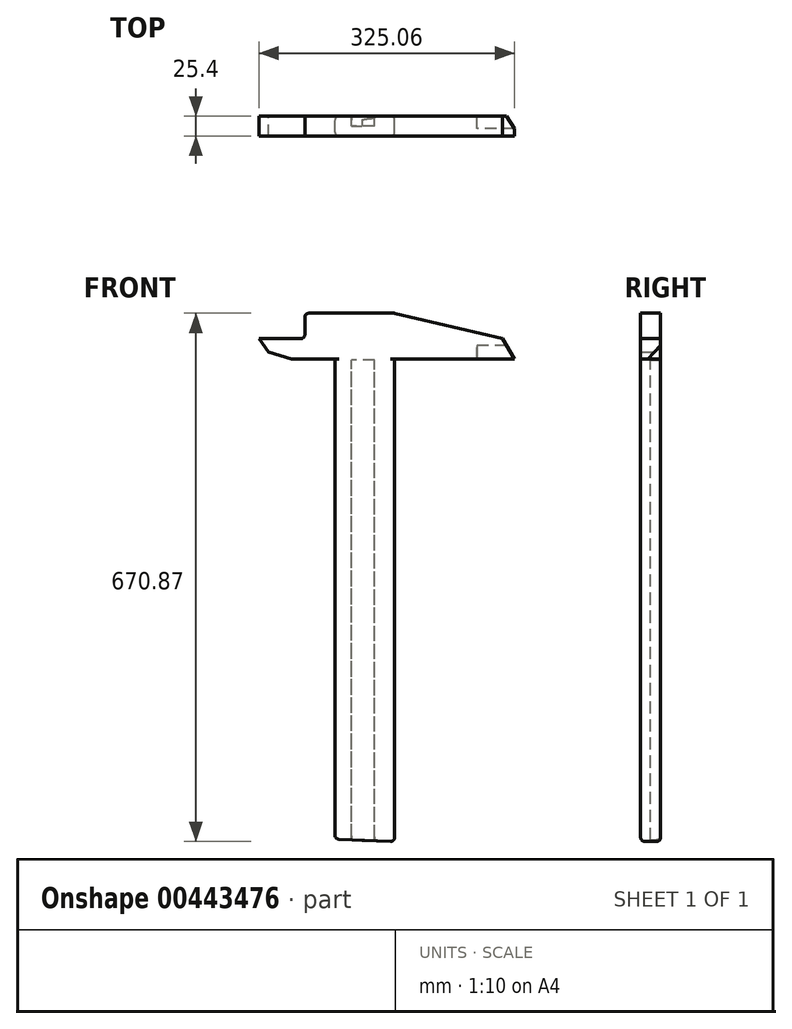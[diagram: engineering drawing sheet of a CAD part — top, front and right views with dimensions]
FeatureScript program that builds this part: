
annotation { "Feature Type Name" : "Feature", "Feature Type Description" : "" }
export const myFeature = defineFeature(function(context is Context, id is Id, definition is map)
    precondition{}
    {
        {
            var Q0;
            Q0=qCreatedBy(makeId("Front.planeOp"),FACE);
            var sketch = newSketch(context, id + "F0", { "sketchPlane" : qUnion([Q0])});
            skLineSegment(sketch, "E0", {"start": v(0, 0) * mm, "end": v(0, 114.3) * mm, "construction": true});
            skLineSegment(sketch, "E1", {"start": v(0, 114.3) * mm, "end": v(-53.98, 114.3) * mm, "construction": true});
            skLineSegment(sketch, "E2", {"start": v(-53.98, 114.3) * mm, "end": v(47.63, 114.3) * mm});
            skLineSegment(sketch, "E3", {"start": v(-53.98, 114.3) * mm, "end": v(-104.78, 114.3) * mm});
            skLineSegment(sketch, "E4", {"start": v(47.63, 114.3) * mm, "end": v(31.96, 140.42) * mm});
            skLineSegment(sketch, "E5", {"start": v(31.96, 140.42) * mm, "end": v(-105.1, 172.67) * mm});
            skLineSegment(sketch, "E6", {"start": v(-105.1, 172.67) * mm, "end": v(-218.99, 172.67) * mm});
            skLineSegment(sketch, "E7", {"start": v(-218.99, 172.67) * mm, "end": v(-218.99, 140.42) * mm});
            skLineSegment(sketch, "E8", {"start": v(-218.99, 140.42) * mm, "end": v(-277.44, 140.42) * mm});
            skLineSegment(sketch, "E9", {"start": v(-277.44, 140.42) * mm, "end": v(-265.35, 123.28) * mm});
            skLineSegment(sketch, "E10", {"start": v(-265.35, 123.28) * mm, "end": v(-235.11, 114.3) * mm});
            skLineSegment(sketch, "E11", {"start": v(-235.11, 114.3) * mm, "end": v(-180.7, 114.3) * mm});
            skLineSegment(sketch, "E12", {"start": v(-180.7, 114.3) * mm, "end": v(-180.7, -292.1) * mm});
            skLineSegment(sketch, "E13", {"start": v(-104.78, -292.1) * mm, "end": v(-104.78, 114.3) * mm});
            skLineSegment(sketch, "E14", {"start": v(-180.7, -292.1) * mm, "end": v(-180.7, -495.3) * mm});
            skLineSegment(sketch, "E15", {"start": v(-104.78, -292.1) * mm, "end": v(-104.77, -498.4) * mm});
            skLineSegment(sketch, "E16", {"start": v(-104.77, -498.4) * mm, "end": v(-180.7, -495.3) * mm});
            skSolve(sketch);
        }
        {
            var Q0;
            Q0=makeQuery(id+"F0.imprint","IMPRINT",FACE,{"disambiguationData":[TD([[makeQuery(id+"F0.imprint","IMPRINT",EDGE,{"derivedFrom":sQuery(id+"F0.wireOp",EDGE,"E2")}),1.0]])]});
            extrude(context, id + "F1", {"entities" : qUnion([Q0]), "depth" : 25.4 * mm});
        }
        {
            var Q0;
            Q0=makeQuery(id+"F1.opExtrude","SWEPT_EDGE",EDGE,{"disambiguationData":[OSD([sQuery(id+"F0.wireOp",EDGE,"E5"),sQuery(id+"F0.wireOp",EDGE,"E6")])]});
            var Q1;
            Q1=makeQuery(id+"F1.opExtrude","SWEPT_EDGE",EDGE,{"disambiguationData":[OSD([sQuery(id+"F0.wireOp",EDGE,"E6"),sQuery(id+"F0.wireOp",EDGE,"E7")])]});
            var Q2;
            Q2=makeQuery(id+"F1.opExtrude","SWEPT_EDGE",EDGE,{"disambiguationData":[OSD([sQuery(id+"F0.wireOp",EDGE,"E7"),sQuery(id+"F0.wireOp",EDGE,"E8")])]});
            var Q3;
            Q3=makeQuery(id+"F1.opExtrude","SWEPT_EDGE",EDGE,{"disambiguationData":[OSD([sQuery(id+"F0.wireOp",EDGE,"E10"),sQuery(id+"F0.wireOp",EDGE,"E11")])]});
            fillet(context, id + "F2", {"entities" : qUnion([Q0, Q1, Q2, Q3]), "radius" : 5.08 * mm, "tangentPropagation" : true, "allowEdgeOverflow" : false});
        }
        {
            var Q0;
            Q0=qCreatedBy(makeId("Right.planeOp"),FACE);
            var sketch = newSketch(context, id + "F3", { "sketchPlane" : qUnion([Q0])});
            skLineSegment(sketch, "E17", {"start": v(0, 0) * mm, "end": v(0, 114.3) * mm});
            skLineSegment(sketch, "E18", {"start": v(0, 114.3) * mm, "end": v(-16.01, 114.3) * mm});
            skLineSegment(sketch, "E19", {"start": v(-16.01, 114.3) * mm, "end": v(0, 131.55) * mm});
            skLineSegment(sketch, "E20", {"start": v(0, 131.55) * mm, "end": v(0, 114.3) * mm});
            skSolve(sketch);
        }
        {
            var Q0;
            Q0 = qSketchRegion(id + "F3", true);
            extrude(context, id + "F4", {"entities" : qUnion([Q0]), "operationType" : NewBodyOperationType.REMOVE, "depth" : 63.5 * mm});
        }
        {
            var Q0;
            Q0=makeQuery(id+"F1.opExtrude","CAP_FACE",FACE,{"disambiguationData":[OSD([sQuery(id+"F0.wireOp",EDGE,"E2"),sQuery(id+"F0.wireOp",EDGE,"E3"),sQuery(id+"F0.wireOp",EDGE,"E4"),sQuery(id+"F0.wireOp",EDGE,"E5"),sQuery(id+"F0.wireOp",EDGE,"E6"),sQuery(id+"F0.wireOp",EDGE,"E7"),sQuery(id+"F0.wireOp",EDGE,"E8"),sQuery(id+"F0.wireOp",EDGE,"E9"),sQuery(id+"F0.wireOp",EDGE,"E10"),sQuery(id+"F0.wireOp",EDGE,"E11"),sQuery(id+"F0.wireOp",EDGE,"E12"),sQuery(id+"F0.wireOp",EDGE,"E13"),sQuery(id+"F0.wireOp",EDGE,"E14"),sQuery(id+"F0.wireOp",EDGE,"E15"),sQuery(id+"F0.wireOp",EDGE,"E16")])],"isStart":true});
            var sketch = newSketch(context, id + "F5", { "sketchPlane" : qUnion([Q0])});
            skLineSegment(sketch, "E21", {"start": v(104.78, 114.3) * mm, "end": v(180.7, 114.3) * mm});
            skSolve(sketch);
        }
        {
            var Q0;
            Q0=makeQuery(id+"F1.opExtrude","CAP_EDGE",EDGE,{"disambiguationData":[OSD([sQuery(id+"F0.wireOp",EDGE,"E13"),sQuery(id+"F0.wireOp",EDGE,"E15")])],"isStart":true});
            var Q1;
            Q1=makeQuery(id+"F1.opExtrude","CAP_EDGE",EDGE,{"disambiguationData":[OSD([sQuery(id+"F0.wireOp",EDGE,"E12"),sQuery(id+"F0.wireOp",EDGE,"E14")])],"isStart":true});
            var Q2;
            Q2=makeQuery(id+"F1.opExtrude","CAP_EDGE",EDGE,{"disambiguationData":[OSD([sQuery(id+"F0.wireOp",EDGE,"E16")])],"isStart":true});
            var Q3;
            Q3=makeQuery(id+"F1.opExtrude","CAP_EDGE",EDGE,{"disambiguationData":[OSD([sQuery(id+"F0.wireOp",EDGE,"E13"),sQuery(id+"F0.wireOp",EDGE,"E15")])],"isStart":false});
            var Q4;
            Q4=makeQuery(id+"F1.opExtrude","CAP_EDGE",EDGE,{"disambiguationData":[OSD([sQuery(id+"F0.wireOp",EDGE,"E12"),sQuery(id+"F0.wireOp",EDGE,"E14")])],"isStart":false});
            var Q5;
            Q5=makeQuery(id+"F1.opExtrude","CAP_EDGE",EDGE,{"disambiguationData":[OSD([sQuery(id+"F0.wireOp",EDGE,"E16")])],"isStart":false});
            var Q6;
            Q6=makeQuery(id+"F1.opExtrude","SWEPT_EDGE",EDGE,{"disambiguationData":[OSD([sQuery(id+"F0.wireOp",EDGE,"E15"),sQuery(id+"F0.wireOp",EDGE,"E16")])]});
            var Q7;
            Q7=makeQuery(id+"F1.opExtrude","SWEPT_EDGE",EDGE,{"disambiguationData":[OSD([sQuery(id+"F0.wireOp",EDGE,"E14"),sQuery(id+"F0.wireOp",EDGE,"E16")])]});
            fillet(context, id + "F6", {"entities" : qUnion([Q0, Q1, Q2, Q3, Q4, Q5, Q6, Q7]), "radius" : 5.08 * mm, "tangentPropagation" : true, "allowEdgeOverflow" : false});
        }
        {
            var Q0;
            Q0=makeQuery(id+"F5.imprint","IMPRINT",FACE,{"disambiguationData":[TD([[makeQuery(id+"F5.imprint","IMPRINT",EDGE,{"derivedFrom":sQuery(id+"F5.wireOp",EDGE,"E21")}),-1.0]])]});
            var sketch = newSketch(context, id + "F7", { "sketchPlane" : qUnion([Q0])});
            skLineSegment(sketch, "E22.bottom", {"start": v(130.19, -496.7) * mm, "end": v(159.75, -496.7) * mm});
            skLineSegment(sketch, "E22.top", {"start": v(130.19, 113.07) * mm, "end": v(159.75, 113.07) * mm});
            skLineSegment(sketch, "E22.left", {"start": v(130.19, -496.7) * mm, "end": v(130.19, 113.07) * mm});
            skLineSegment(sketch, "E22.right", {"start": v(159.75, -496.7) * mm, "end": v(159.75, 113.07) * mm});
            skSolve(sketch);
        }
        {
            var Q0;
            Q0 = qSketchRegion(id + "F7", true);
            extrude(context, id + "F8", {"entities" : qUnion([Q0]), "operationType" : NewBodyOperationType.REMOVE, "oppositeDirection" : true, "depth" : 12.7 * mm});
        }
    });
